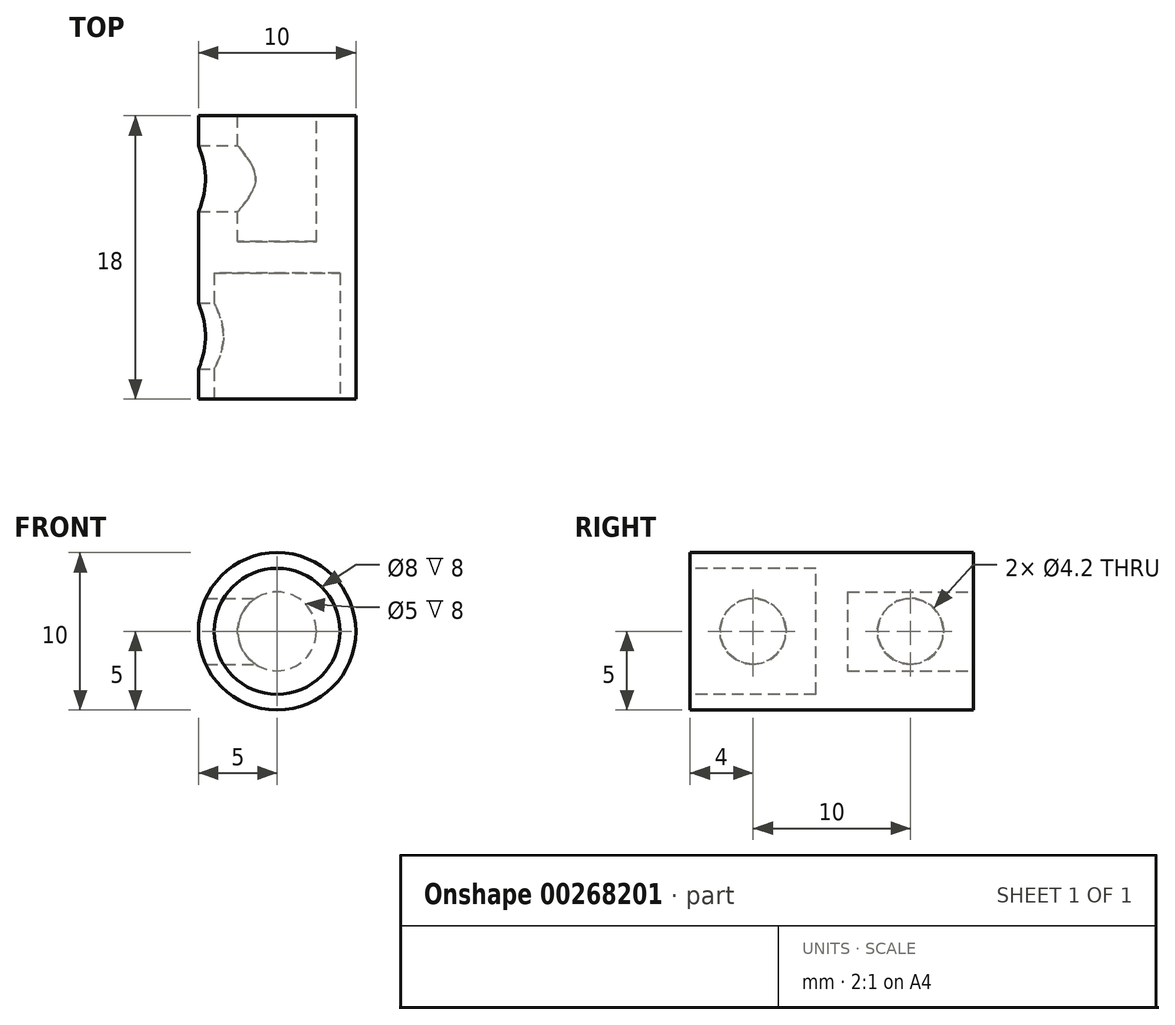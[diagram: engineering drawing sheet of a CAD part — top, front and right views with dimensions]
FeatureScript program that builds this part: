
annotation { "Feature Type Name" : "Feature", "Feature Type Description" : "" }
export const myFeature = defineFeature(function(context is Context, id is Id, definition is map)
    precondition{}
    {
        {
            var Q0;
            Q0=qCreatedBy(makeId("Front.planeOp"),FACE);
            var sketch = newSketch(context, id + "F0", { "sketchPlane" : qUnion([Q0])});
            skCircle(sketch, "E0", {"center": v(0, 0) * mm, "radius": 5 * mm});
            skSolve(sketch);
        }
        {
            var Q0;
            Q0=makeQuery(id+"F0.imprint","IMPRINT",FACE,{"disambiguationData":[TD([[makeQuery(id+"F0.imprint","IMPRINT",EDGE,{"derivedFrom":sQuery(id+"F0.wireOp",EDGE,"E0")}),1.0]])]});
            extrude(context, id + "F1", {"entities" : qUnion([Q0]), "depth" : 18 * mm});
        }
        {
            var Q0;
            Q0=makeQuery(id+"F1.opExtrude","CAP_FACE",FACE,{"disambiguationData":[OSD([sQuery(id+"F0.wireOp",EDGE,"E0")])],"isStart":false});
            var sketch = newSketch(context, id + "F2", { "sketchPlane" : qUnion([Q0])});
            skCircle(sketch, "E1", {"center": v(0, 0) * mm, "radius": 4 * mm});
            skSolve(sketch);
        }
        {
            var Q0;
            Q0=makeQuery(id+"F2.imprint","IMPRINT",FACE,{"disambiguationData":[TD([[makeQuery(id+"F2.imprint","IMPRINT",EDGE,{"derivedFrom":sQuery(id+"F2.wireOp",EDGE,"E1")}),1.0]])]});
            extrude(context, id + "F3", {"entities" : qUnion([Q0]), "operationType" : NewBodyOperationType.REMOVE, "oppositeDirection" : true, "depth" : 8 * mm});
        }
        {
            var Q0;
            Q0=makeQuery(id+"F1.opExtrude","CAP_FACE",FACE,{"disambiguationData":[OSD([sQuery(id+"F0.wireOp",EDGE,"E0")])],"isStart":true});
            var sketch = newSketch(context, id + "F4", { "sketchPlane" : qUnion([Q0])});
            skCircle(sketch, "E2", {"center": v(0, 0) * mm, "radius": 2.5 * mm});
            skSolve(sketch);
        }
        {
            var Q0;
            Q0=makeQuery(id+"F4.imprint","IMPRINT",FACE,{"disambiguationData":[TD([[makeQuery(id+"F4.imprint","IMPRINT",EDGE,{"derivedFrom":sQuery(id+"F4.wireOp",EDGE,"E2")}),1.0]])]});
            extrude(context, id + "F5", {"entities" : qUnion([Q0]), "operationType" : NewBodyOperationType.REMOVE, "oppositeDirection" : true, "depth" : 8 * mm});
        }
        {
            var Q0;
            Q0=qCreatedBy(makeId("Right.planeOp"),FACE);
            var sketch = newSketch(context, id + "F6", { "sketchPlane" : qUnion([Q0])});
            skCircle(sketch, "E3", {"center": v(-14, 0) * mm, "radius": 2 * mm});
            skCircle(sketch, "E4", {"center": v(-4, 0) * mm, "radius": 2 * mm});
            skLineSegment(sketch, "E5", {"start": v(-5.4, 5) * mm, "end": v(-12.85, 5) * mm});
            skSolve(sketch);
        }
        {
            var Q0;
            Q0=sQuery(id+"F6.wireOp",VERTEX,"E4.center");
            var Q1;
            Q1=makeQuery(id+"F1.opExtrude","SWEPT_BODY",BODY,{"disambiguationData":[OSD([sQuery(id+"F0.wireOp",EDGE,"E0")])]});
            hole(context, id + "F7", {"style" : HoleStyle.SIMPLE, "endStyle" : HoleEndStyle.BLIND, "standardTappedOrClearance" : lookupTablePath({ "standard" : "ISO", "engagement" : "75%", "pitch" : "0.8 mm", "size" : "M5", "type" : "Tapped" }), "standardBlindInLast" : lookupTablePath({ "standard" : "ISO", "engagement" : "75%", "pitch" : "0.8 mm", "size" : "M5", "type" : "Tapped" }), "holeDiameter" : 4.2 * mm, "showTappedDepth" : true, "holeDepth" : 14.4 * mm, "tappedDepth" : 12 * mm, "tapClearance" : 3, "locations" : qUnion([Q0]), "scope" : qUnion([Q1]), "majorDiameter" : 5 * mm});
        }
        {
            var Q0;
            Q0=sQuery(id+"F6.wireOp",VERTEX,"E3.center");
            var Q1;
            Q1=makeQuery(id+"F1.opExtrude","SWEPT_BODY",BODY,{"disambiguationData":[OSD([sQuery(id+"F0.wireOp",EDGE,"E0")])]});
            hole(context, id + "F8", {"style" : HoleStyle.SIMPLE, "endStyle" : HoleEndStyle.BLIND, "standardTappedOrClearance" : lookupTablePath({ "standard" : "ISO", "engagement" : "75%", "pitch" : "0.8 mm", "size" : "M5", "type" : "Tapped" }), "standardBlindInLast" : lookupTablePath({ "standard" : "ISO", "engagement" : "75%", "pitch" : "0.8 mm", "size" : "M5", "type" : "Tapped" }), "holeDiameter" : 4.2 * mm, "showTappedDepth" : true, "holeDepth" : 14.4 * mm, "tappedDepth" : 12 * mm, "tapClearance" : 3, "locations" : qUnion([Q0]), "scope" : qUnion([Q1]), "majorDiameter" : 5 * mm});
        }
    });
